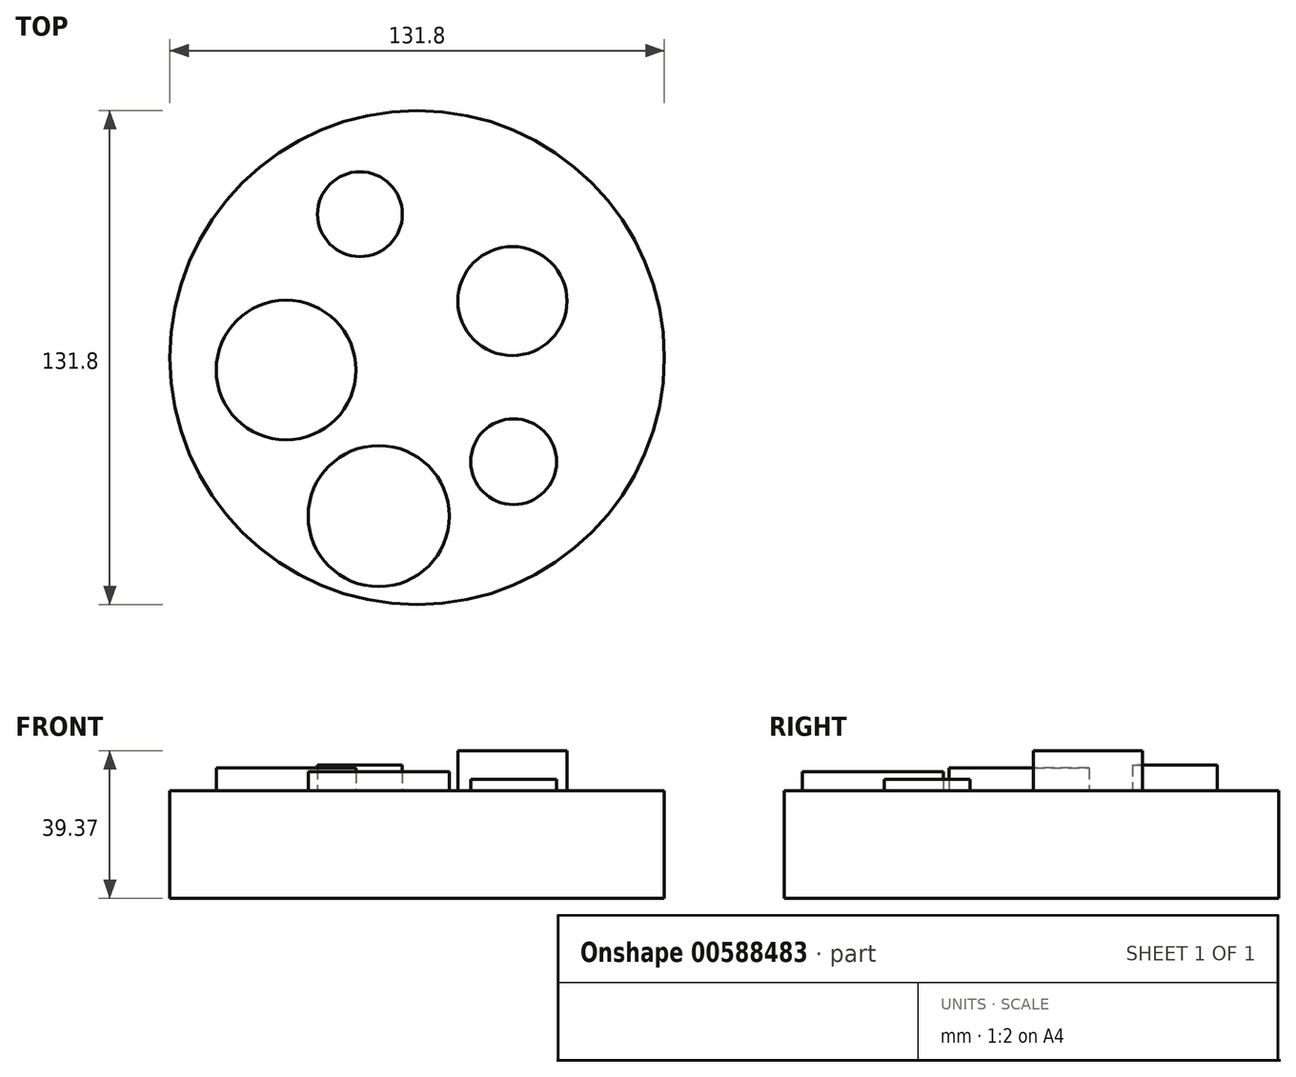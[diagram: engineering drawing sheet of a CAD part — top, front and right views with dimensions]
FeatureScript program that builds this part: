
annotation { "Feature Type Name" : "Feature", "Feature Type Description" : "" }
export const myFeature = defineFeature(function(context is Context, id is Id, definition is map)
    precondition{}
    {
        {
            var Q0;
            Q0=qCreatedBy(makeId("Top.planeOp"),FACE);
            var sketch = newSketch(context, id + "F0", { "sketchPlane" : qUnion([Q0])});
            skCircle(sketch, "E0", {"center": v(0, 0) * mm, "radius": 65.9 * mm});
            skSolve(sketch);
        }
        {
            var Q0;
            Q0=makeQuery(id+"F0.imprint","IMPRINT",FACE,{"disambiguationData":[TD([[makeQuery(id+"F0.imprint","IMPRINT",EDGE,{"derivedFrom":sQuery(id+"F0.wireOp",EDGE,"E0")}),1.0]])]});
            extrude(context, id + "F1", {"entities" : qUnion([Q0]), "oppositeDirection" : true, "depth" : 28.7 * mm, "offsetDistance" : 25.4 * mm});
        }
        {
            var Q0;
            Q0=qCreatedBy(makeId("Top.planeOp"),FACE);
            var sketch = newSketch(context, id + "F2", { "sketchPlane" : qUnion([Q0])});
            skCircle(sketch, "E1", {"center": v(-15.24, 38.26) * mm, "radius": 11.3 * mm});
            skSolve(sketch);
        }
        {
            var Q0;
            Q0 = qSketchRegion(id + "F2", true);
            extrude(context, id + "F3", {"entities" : qUnion([Q0]), "operationType" : NewBodyOperationType.ADD, "depth" : 6.86 * mm, "offsetDistance" : 25.4 * mm});
        }
        {
            var Q0;
            Q0=qCreatedBy(makeId("Top.planeOp"),FACE);
            var sketch = newSketch(context, id + "F4", { "sketchPlane" : qUnion([Q0])});
            skCircle(sketch, "E2", {"center": v(-34.92, -3.33) * mm, "radius": 18.64 * mm});
            skSolve(sketch);
        }
        {
            var Q0;
            Q0 = qSketchRegion(id + "F4", true);
            extrude(context, id + "F5", {"entities" : qUnion([Q0]), "operationType" : NewBodyOperationType.ADD, "depth" : 6.1 * mm, "offsetDistance" : 25.4 * mm});
        }
        {
            var Q0;
            Q0=qCreatedBy(makeId("Top.planeOp"),FACE);
            var sketch = newSketch(context, id + "F6", { "sketchPlane" : qUnion([Q0])});
            skCircle(sketch, "E3", {"center": v(25.4, 15.08) * mm, "radius": 14.54 * mm});
            skSolve(sketch);
        }
        {
            var Q0;
            Q0 = qSketchRegion(id + "F6", true);
            extrude(context, id + "F7", {"entities" : qUnion([Q0]), "operationType" : NewBodyOperationType.ADD, "depth" : 10.67 * mm, "offsetDistance" : 25.4 * mm});
        }
        {
            var Q0;
            Q0=qCreatedBy(makeId("Top.planeOp"),FACE);
            var sketch = newSketch(context, id + "F8", { "sketchPlane" : qUnion([Q0])});
            skCircle(sketch, "E4", {"center": v(25.72, -27.78) * mm, "radius": 11.45 * mm});
            skSolve(sketch);
        }
        {
            var Q0;
            Q0 = qSketchRegion(id + "F8", true);
            extrude(context, id + "F9", {"entities" : qUnion([Q0]), "operationType" : NewBodyOperationType.ADD, "depth" : 3.05 * mm, "offsetDistance" : 25.4 * mm});
        }
        {
            var Q0;
            Q0=qCreatedBy(makeId("Top.planeOp"),FACE);
            var sketch = newSketch(context, id + "F10", { "sketchPlane" : qUnion([Q0])});
            skCircle(sketch, "E5", {"center": v(-10.23, -42.3) * mm, "radius": 18.82 * mm});
            skSolve(sketch);
        }
        {
            var Q0;
            Q0 = qSketchRegion(id + "F10", true);
            extrude(context, id + "F11", {"entities" : qUnion([Q0]), "operationType" : NewBodyOperationType.ADD, "depth" : 5.08 * mm, "offsetDistance" : 25.4 * mm});
        }
    });
